# Revit family: Gewindestangen 1 m, fvz
name_source: partatom
category: HLS-Bauteile
revit_build: Autodesk Revit 2017 (Build: 20190507_1515(x64)
units: mm (PartAtom-declared; Revit-internal decimal feet)

## family parameters
Arbeitsebenenbasiert = Nein
Beim Laden mit Abzugskörper schneiden = Nein
Bemaßung runder Anschluss = Durchmesser verwenden
Gemeinsam genutzt = Ja
Immer vertikal = Nein
Raumberechnungspunkt = Nein
Teiletyp = Normal

## types (3) — shared parameters
Fabrikat = MEFA
Festigkeitsklasse = 8.8
Kurztext1 = Gewindestange DIN 976-1
Länge = 1000 mm  [stored 3.28084 ft]
Material = Stahl
Mengeneinheit = St
Montagelänge = 1000 mm  [stored 3.28084 ft]

## per-type parameters (varying)
| type | Artikelnummer | D | EAN | Gewicht | Gewicht pro Bauteil | Gewicht pro Stück | Gewinde | Kurztext2 | vpe |
| Gewindestange M10x1000, fvz | 0739103/fvz | 8 mm  [stored 0.0262467 ft] | 4250928457059 | 0.51 kg | 0.51 kg | 0.51 kg | M10 | M10 x 1000 mm fvz FK 8.8 | 25 St |
| Gewindestange M12x1000, fvz | 0739137/fvz | 10 mm  [stored 0.0328084 ft] | 4250928457066 | 0.74 kg | 0.74 kg | 0.74 kg | M12 | M12 x 1000 mm fvz FK 8.8 | 25 St |
| Gewindestange M16x1000, fvz | 0739162/fvz | 14 mm  [stored 0.0459318 ft] | 4250928457073 | 1.31 kg | 1.31 kg | 1.31 kg | M16 | M16 x 1000 mm fvz FK 8.8 | 10 St |

note: [stored X ft] marks values corroborated as IEEE doubles in the binary element streams (Revit-internal decimal feet)
